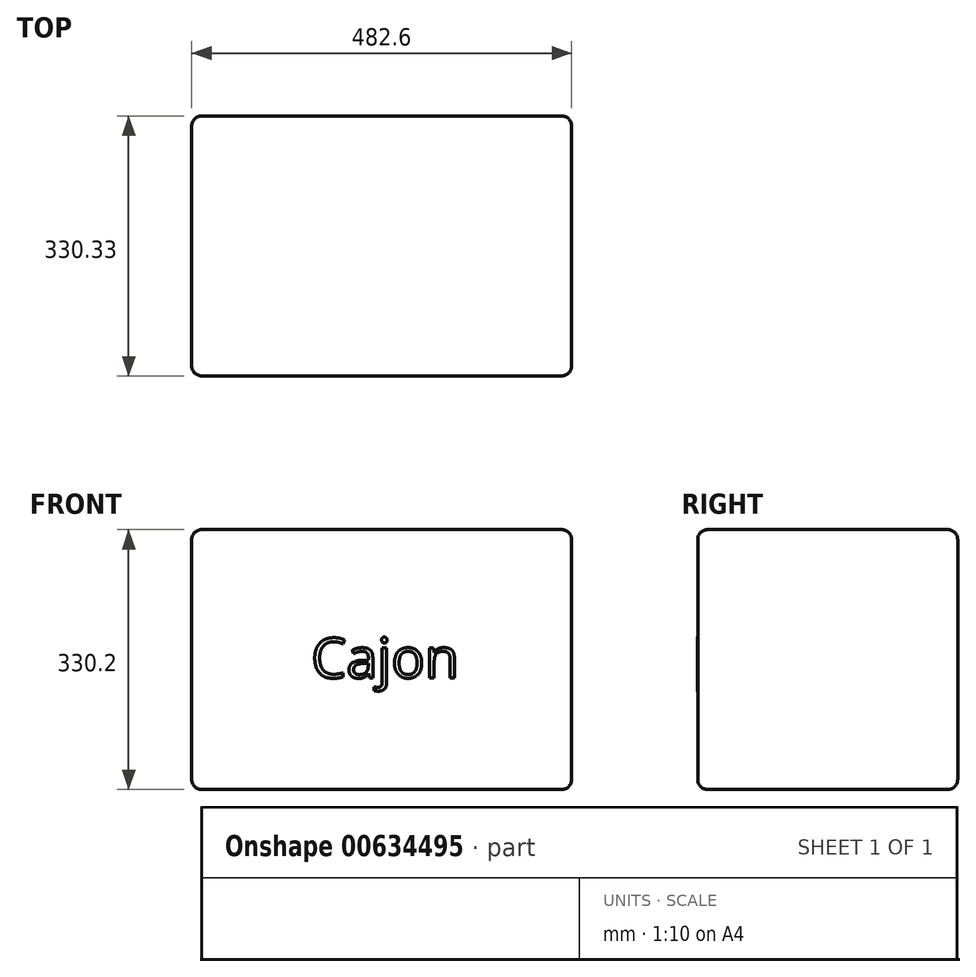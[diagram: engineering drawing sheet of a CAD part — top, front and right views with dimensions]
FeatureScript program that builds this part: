
annotation { "Feature Type Name" : "Feature", "Feature Type Description" : "" }
export const myFeature = defineFeature(function(context is Context, id is Id, definition is map)
    precondition{}
    {
        {
            var Q0;
            Q0=qCreatedBy(makeId("Top.planeOp"),FACE);
            var sketch = newSketch(context, id + "F0", { "sketchPlane" : qUnion([Q0])});
            skLineSegment(sketch, "E0.bottom", {"start": v(-241.3, 165.1) * mm, "end": v(241.3, 165.1) * mm});
            skLineSegment(sketch, "E0.top", {"start": v(-241.3, -165.1) * mm, "end": v(241.3, -165.1) * mm});
            skLineSegment(sketch, "E0.left", {"start": v(-241.3, 165.1) * mm, "end": v(-241.3, -165.1) * mm});
            skLineSegment(sketch, "E0.right", {"start": v(241.3, 165.1) * mm, "end": v(241.3, -165.1) * mm});
            skPoint(sketch, "E0.middle", {"position": v(0, 0) * mm});
            skSolve(sketch);
        }
        {
            var Q0;
            Q0=makeQuery(id+"F0.imprint","IMPRINT",FACE,{"disambiguationData":[TD([[makeQuery(id+"F0.imprint","IMPRINT",EDGE,{"derivedFrom":sQuery(id+"F0.wireOp",EDGE,"E0.bottom")}),-1.0]])]});
            extrude(context, id + "F1", {"entities" : qUnion([Q0]), "depth" : 330.2 * mm, "offsetDistance" : 25.4 * mm});
        }
        {
            var Q0;
            Q0=makeQuery(id+"F1.opExtrude","CAP_FACE",FACE,{"disambiguationData":[OSD([sQuery(id+"F0.wireOp",EDGE,"E0.bottom"),sQuery(id+"F0.wireOp",EDGE,"E0.top"),sQuery(id+"F0.wireOp",EDGE,"E0.left"),sQuery(id+"F0.wireOp",EDGE,"E0.right")])],"isStart":false});
            var Q1;
            Q1=makeQuery(id+"F1.opExtrude","SWEPT_FACE",FACE,{"disambiguationData":[OSD([sQuery(id+"F0.wireOp",EDGE,"E0.right")])]});
            var Q2;
            Q2=makeQuery(id+"F1.opExtrude","SWEPT_FACE",FACE,{"disambiguationData":[OSD([sQuery(id+"F0.wireOp",EDGE,"E0.top")])]});
            var Q3;
            Q3=makeQuery(id+"F1.opExtrude","SWEPT_FACE",FACE,{"disambiguationData":[OSD([sQuery(id+"F0.wireOp",EDGE,"E0.left")])]});
            var Q4;
            Q4=makeQuery(id+"F1.opExtrude","SWEPT_FACE",FACE,{"disambiguationData":[OSD([sQuery(id+"F0.wireOp",EDGE,"E0.bottom")])]});
            fillet(context, id + "F2", {"entities" : qUnion([Q0, Q1, Q2, Q3, Q4]), "radius" : 12.7 * mm, "tangentPropagation" : true, "allowEdgeOverflow" : false});
        }
        {
            var Q0;
            Q0=makeQuery(id+"F1.opExtrude","SWEPT_FACE",FACE,{"disambiguationData":[OSD([sQuery(id+"F0.wireOp",EDGE,"E0.top")])]});
            var sketch = newSketch(context, id + "F3", { "sketchPlane" : qUnion([Q0])});
            skText(sketch, "E1", { "text": "Cajon", "fontName": "OpenSans-Regular.ttf"});
            const initialGuessF3  = {"E1": [-0.08938, 0.1418, 1, 0, 0.0508]};
            skSetInitialGuess(sketch, initialGuessF3);
            skSolve(sketch);
        }
        {
            var Q0;
            Q0 = qSketchRegion(id + "F3", true);
            var Q1;
            Q1 = qConstructionFilter(qBodyType(qCreatedBy(id + "F3" ,EDGE), BodyType.WIRE), ConstructionObject.NO);
            extrude(context, id + "F4", {"entities" : qUnion([Q0]), "operationType" : NewBodyOperationType.ADD, "surfaceEntities" : qUnion([Q1]), "depth" : 0.13 * mm, "offsetDistance" : 25.4 * mm});
        }
    });
